# Revit family: Skylight-Wasco-CSP-Pyramid_Dome
name_source: partatom
category: Windows
revit_build: Autodesk Revit Architecture 2013 (Build: 20130531_2115(x64)
units: mm (PartAtom-declared; Revit-internal decimal feet)

## types (19) — shared parameters
A = 11.02°
Acrylic Glazing Inner = Acrylic - Wasco - Clear
Acrylic Glazing Outer = Acrylic - Wasco - Clear
Curb = Rubber, Black
Curb Height = 0' - 3 1/2"
Curb Width = 0' - 1 1/2"
Default Elevation = 0' - 0"
Description = Skylight
Finish = Aluminum - Wasco - Aged Copper
Host Constraint = 1
Manufacturer = Wasco
Overhang = 0' - 1 25/32"
Product Documentation Link = http://www.wascoskylights.com
Product Name = CSP Pyramid Dome
Product Page URL = http://www.wascoskylights.com
Type Comments = Maximum length and width = 95.5in x 95.5in.  Long leg to short leg maximum ratio cannot be more than 2.3.
URL = http://www.wascoskylights.com

## per-type parameters (varying)
| type | Altitude | Height | Host Length | Host Width | L | Length | Model | Rough Height | Rough Length | Rough Width | Width |
| DDCS2424 | 0' - 2 5/16" | 0' - 2 5/16" | 3' - 10" | 3' - 10" | 0' - 11 7/8" | 1' - 10" | DDCSP2424 | 0' - 7 1/32" | 1' - 11 25/32" | 1' - 11 25/32" | 1' - 10" |
| DDCSP2828 | 0' - 2 5/8" | 0' - 2 5/8" | 4' - 1 1/4" | 4' - 1 1/4" | 1' - 1 1/2" | 2' - 1 1/4" | DDCSP2828 | 0' - 7 11/32" | 2' - 3 1/32" | 2' - 3 1/32" | 2' - 1 1/4" |
| DDCSP2836 | 0' - 2 5/8" | 0' - 2 5/8" | 4' - 9 1/4" | 4' - 1 1/4" | 1' - 1 1/2" | 2' - 9 1/4" | DDCSP2836 | 0' - 7 11/32" | 2' - 11 1/32" | 2' - 3 1/32" | 2' - 1 1/4" |
| DDCSP2852 | 0' - 2 5/8" | 0' - 2 5/8" | 6' - 1 1/4" | 4' - 1 1/4" | 1' - 1 1/2" | 4' - 1 1/4" | DDCSP2852 | 0' - 7 11/32" | 4' - 3 1/32" | 2' - 3 1/32" | 2' - 1 1/4" |
| DDCSP3636 | 0' - 3 13/32" | 0' - 3 13/32" | 4' - 9 1/4" | 4' - 9 1/4" | 1' - 5 1/2" | 2' - 9 1/4" | DDCSP3636 | 0' - 8 1/8" | 2' - 11 1/32" | 2' - 11 1/32" | 2' - 9 1/4" |
| DDCSP3652 | 0' - 3 13/32" | 0' - 3 13/32" | 6' - 0 1/4" | 4' - 9 1/4" | 1' - 5 1/2" | 4' - 0 1/4" | DDCSP3652 | 0' - 8 1/8" | 4' - 2 1/32" | 2' - 11 1/32" | 2' - 9 1/4" |
| DDCSP3676 | 0' - 3 13/32" | 0' - 3 13/32" | 8' - 0 1/2" | 4' - 9 1/4" | 1' - 5 1/2" | 6' - 0 1/2" | DDCSP3676 | 0' - 8 1/8" | 6' - 2 9/32" | 2' - 11 1/32" | 2' - 9 1/4" |
| DDCSP4242 | 0' - 4 1/16" | 0' - 4 1/16" | 5' - 4" | 5' - 4" | 1' - 8 7/8" | 3' - 4" | DDCCP4242 | 0' - 8 25/32" | 3' - 5 25/32" | 3' - 5 25/32" | 3' - 4" |
| DDCSP4280 | 0' - 4 1/16" | 0' - 4 1/16" | 8' - 6" | 5' - 4" | 1' - 8 7/8" | 6' - 6" | DDCSP4280 | 0' - 8 25/32" | 6' - 7 25/32" | 3' - 5 25/32" | 3' - 4" |
| DDCSP5252 | 0' - 4 31/32" | 0' - 4 31/32" | 6' - 1 1/4" | 6' - 1 1/4" | 2' - 1 1/2" | 4' - 1 1/4" | DDCSP5252 | 0' - 9 11/16" | 4' - 3 1/32" | 4' - 3 1/32" | 4' - 1 1/4" |
| DDCSP5276 | 0' - 4 31/32" | 0' - 4 31/32" | 8' - 0 1/2" | 6' - 1 1/4" | 2' - 1 1/2" | 6' - 0 1/2" | DDCSP5276 | 0' - 9 11/16" | 6' - 2 9/32" | 4' - 3 1/32" | 4' - 1 1/4" |
| DDCSP5296 | 0' - 4 31/32" | 0' - 4 31/32" | 9' - 8 1/2" | 6' - 1 1/4" | 2' - 1 1/2" | 7' - 8 1/2" | DDCSP5296 | 0' - 9 11/16" | 7' - 10 9/32" | 4' - 3 1/32" | 4' - 1 1/4" |
| DDCSP6060 | 0' - 5 13/16" | 0' - 5 13/16" | 6' - 10" | 6' - 10" | 2' - 5 7/8" | 4' - 10" | DDCSP6060 | 0' - 10 17/32" | 4' - 11 25/32" | 4' - 11 25/32" | 4' - 10" |
| DDCSP6476 | 0' - 6 1/16" | 0' - 6 1/16" | 8' - 0 1/2" | 7' - 0 1/2" | 2' - 7 1/8" | 6' - 0 1/2" | DDCSP6476 | 0' - 10 25/32" | 6' - 2 9/32" | 5' - 2 9/32" | 5' - 0 1/2" |
| DDCSP6496 | 0' - 6 1/16" | 0' - 6 1/16" | 9' - 8 1/2" | 7' - 0 1/2" | 2' - 7 1/8" | 7' - 8 1/2" | DDCSP6496 | 0' - 10 25/32" | 7' - 10 9/32" | 5' - 2 9/32" | 5' - 0 1/2" |
| DDCSP7272 | 0' - 7 3/32" | 0' - 7 3/32" | 7' - 11" | 7' - 11" | 3' - 0 3/8" | 5' - 11" | DDCSP7272 | 0' - 11 13/16" | 6' - 0 25/32" | 6' - 0 25/32" | 5' - 11" |
| DDCSP8080 | 0' - 7 3/4" | 0' - 7 3/4" | 8' - 6" | 8' - 6" | 3' - 3 7/8" | 6' - 6" | DDCSP8080 | 1' - 0 15/32" | 6' - 7 25/32" | 6' - 7 25/32" | 6' - 6" |
| DDCSP9898 | 0' - 9 15/32" | 0' - 9 15/32" | 9' - 11 1/2" | 9' - 11 1/2" | 4' - 0 5/8" | 7' - 11 1/2" | DDCSP9898 | 1' - 2 3/16" | 8' - 1 9/32" | 8' - 1 9/32" | 7' - 11 1/2" |
| Custom | 0' - 4 27/32" | 0' - 4 27/32" | 6' - 0" | 6' - 0" | 2' - 0 7/8" | 4' - 0" | Custom | 0' - 9 9/16" | 4' - 1 25/32" | 4' - 1 25/32" | 4' - 0" |

## geometry (parser evidence)
native form markers: Blend x23, Extrusion x1, Sweep x3
no freeform markers — native parametric forms only
